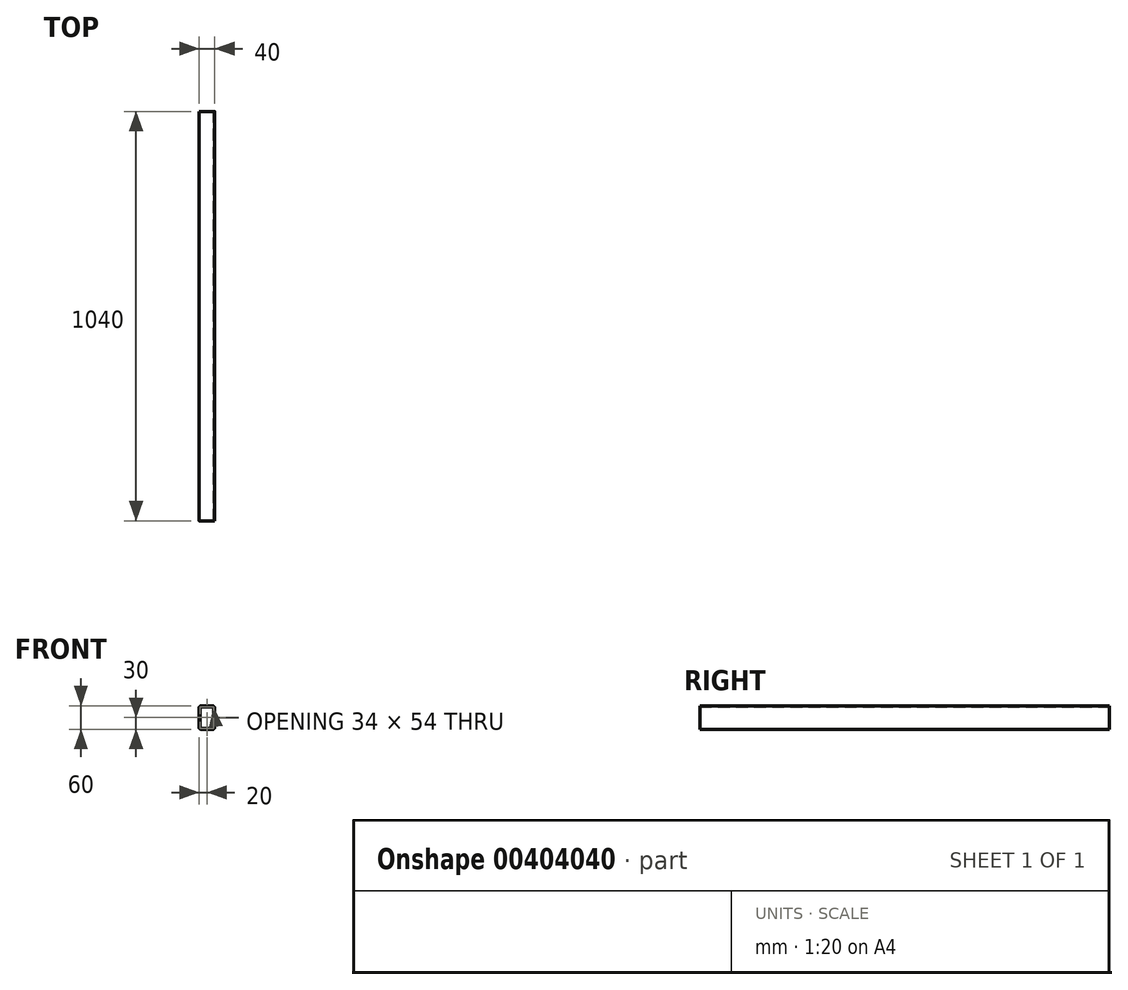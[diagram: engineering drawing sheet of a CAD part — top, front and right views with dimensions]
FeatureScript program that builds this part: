
annotation { "Feature Type Name" : "Feature", "Feature Type Description" : "" }
export const myFeature = defineFeature(function(context is Context, id is Id, definition is map)
    precondition{}
    {
        {
            var Q0;
            Q0=qCreatedBy(makeId("Front.planeOp"),FACE);
            var sketch = newSketch(context, id + "F0", { "sketchPlane" : qUnion([Q0])});
            skLineSegment(sketch, "E0.bottom", {"start": v(-14, 30) * mm, "end": v(14, 30) * mm});
            skLineSegment(sketch, "E0.top", {"start": v(-14, -30) * mm, "end": v(14, -30) * mm});
            skLineSegment(sketch, "E0.left", {"start": v(-20, 24) * mm, "end": v(-20, -24) * mm});
            skLineSegment(sketch, "E0.right", {"start": v(20, 24) * mm, "end": v(20, -24) * mm});
            skPoint(sketch, "E1.visualSharp", {"position": v(-20, 30) * mm});
            skArc(sketch, "E1.filletArc", {"start": v(-14, 30) * mm, "mid": v(-18.24, 28.24) * mm, "end": v(-20, 24) * mm});
            skPoint(sketch, "E2.visualSharp", {"position": v(-20, -30) * mm});
            skArc(sketch, "E2.filletArc", {"start": v(-20, -24) * mm, "mid": v(-18.24, -28.24) * mm, "end": v(-14, -30) * mm});
            skPoint(sketch, "E3.visualSharp", {"position": v(20, -30) * mm});
            skArc(sketch, "E3.filletArc", {"start": v(14, -30) * mm, "mid": v(18.24, -28.24) * mm, "end": v(20, -24) * mm});
            skPoint(sketch, "E4.visualSharp", {"position": v(20, 30) * mm});
            skArc(sketch, "E4.filletArc", {"start": v(20, 24) * mm, "mid": v(18.24, 28.24) * mm, "end": v(14, 30) * mm});
            skLineSegment(sketch, "E5.0", {"start": v(-17, 24) * mm, "end": v(-17, -24) * mm});
            skLineSegment(sketch, "E6.0", {"start": v(-14, 27) * mm, "end": v(14, 27) * mm});
            skArc(sketch, "E6.1", {"start": v(17, 24) * mm, "mid": v(16.12, 26.12) * mm, "end": v(14, 27) * mm});
            skLineSegment(sketch, "E6.2", {"start": v(17, 24) * mm, "end": v(17, -24) * mm});
            skArc(sketch, "E6.4", {"start": v(-17, -24) * mm, "mid": v(-16.12, -26.12) * mm, "end": v(-14, -27) * mm});
            skLineSegment(sketch, "E6.5", {"start": v(-14, -27) * mm, "end": v(14, -27) * mm});
            skArc(sketch, "E6.6", {"start": v(14, -27) * mm, "mid": v(16.12, -26.12) * mm, "end": v(17, -24) * mm});
            skArc(sketch, "E7.0", {"start": v(-14, 27) * mm, "mid": v(-16.12, 26.12) * mm, "end": v(-17, 24) * mm});
            skSolve(sketch);
        }
        {
            var Q0;
            Q0=makeQuery(id+"F0.imprint","IMPRINT",FACE,{"disambiguationData":[TD([[makeQuery(id+"F0.imprint","IMPRINT",EDGE,{"derivedFrom":sQuery(id+"F0.wireOp",EDGE,"E0.bottom")}),-1.0]])]});
            extrude(context, id + "F1", {"entities" : qUnion([Q0]), "depth" : 1040 * mm});
        }
    });
